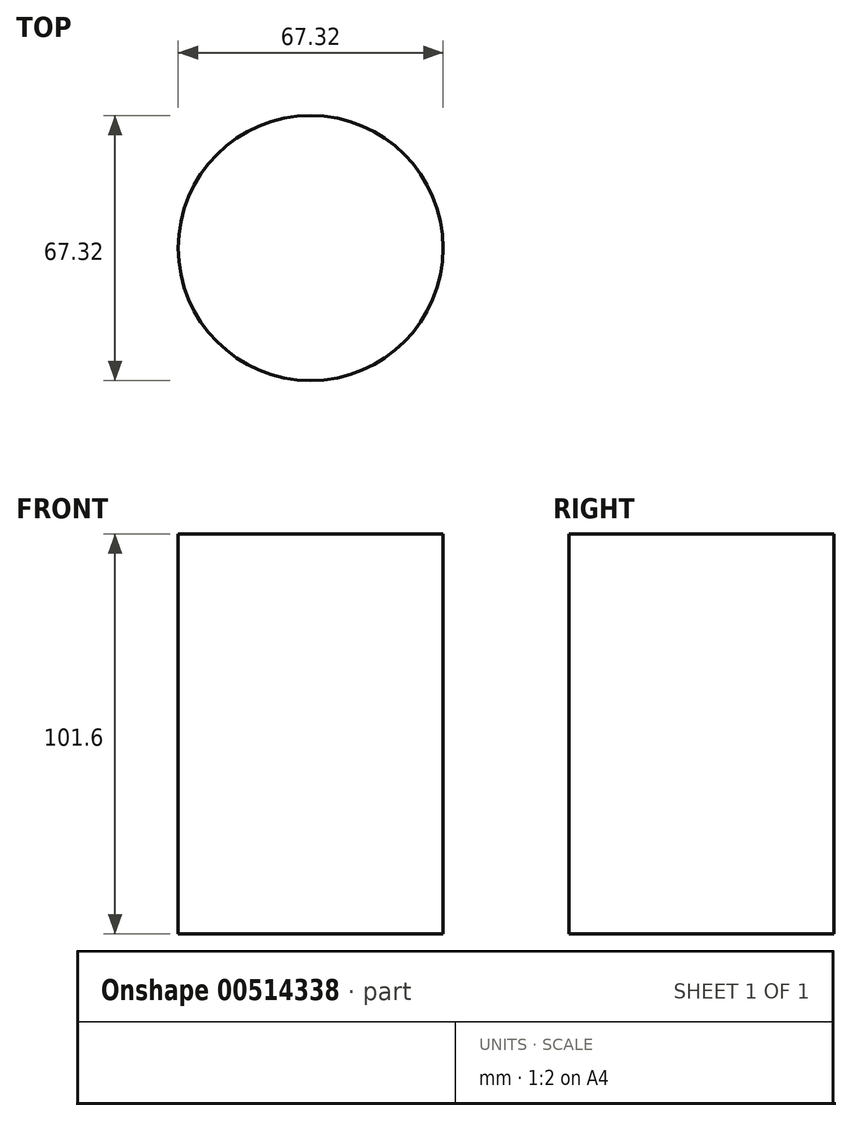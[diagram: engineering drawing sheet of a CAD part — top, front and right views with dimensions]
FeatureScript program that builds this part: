
annotation { "Feature Type Name" : "Feature", "Feature Type Description" : "" }
export const myFeature = defineFeature(function(context is Context, id is Id, definition is map)
    precondition{}
    {
        {
            var Q0;
            Q0=qCreatedBy(makeId("Top.planeOp"),FACE);
            var sketch = newSketch(context, id + "F0", { "sketchPlane" : qUnion([Q0])});
            skCircle(sketch, "E0", {"center": v(0, 0) * mm, "radius": 33.66 * mm});
            skSolve(sketch);
        }
        {
            var Q0;
            Q0=makeQuery(id+"F0.imprint","IMPRINT",FACE,{"disambiguationData":[TD([[makeQuery(id+"F0.imprint","IMPRINT",EDGE,{"derivedFrom":sQuery(id+"F0.wireOp",EDGE,"E0")}),1.0]])]});
            extrude(context, id + "F1", {"entities" : qUnion([Q0]), "depth" : 101.6 * mm, "offsetDistance" : 25.4 * mm});
        }
    });
